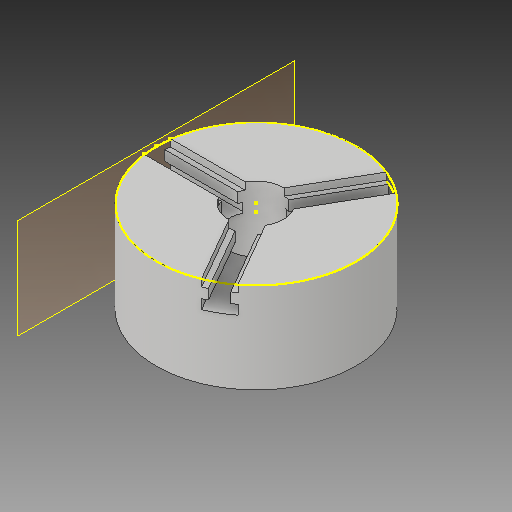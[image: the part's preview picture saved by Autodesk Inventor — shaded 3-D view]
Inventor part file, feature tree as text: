
AUTODESK INVENTOR PART (.ipt)
format: ipt  version: 2018 (Build 220112000, 112)  size: 259,584 bytes
history: native  units: in
note: dims shown in document units (in); Inventor stores cm internally (conversion verified against a paired STEP export)
features: sketch x13, extrude x11, plane x1, pattern_circular x1, projected_geometry x1
ambient origin geometry x8: Origin, YZ Plane, XZ Plane, XY Plane, X Axis, Y Axis, Z Axis, Center Point
bodies: Solid1 (feature_tree)
feature tree (27):
  extrude  "Extrusion1"  Depth=3.5787in
  extrude  "Extrusion2"  Depth=3.5787in
  sketch  "Sketch3"  dims[d13=1.1811in d15=360.0deg d17=0.2827in d18=0.0in]
  extrude  "Extrusion6"  Depth=0.2827in TaperAngle=0.0deg
  extrude  "Extrusion7"  Depth=0.3937in TaperAngle=0.0deg
  extrude  "Extrusion8"  Depth=0.3937in TaperAngle=0.0deg
  extrude  "Extrusion9"  Depth=0.3748in TaperAngle=0.0deg
  extrude  "Extrusion10"  Depth=0.3937in TaperAngle=0.0deg
  sketch  "Sketch12"  dims[d43=1.1811in d44=360.0deg d48=1.1811in d50=360.0deg]
  sketch  "Sketch13"  dims[d52=1.9685in d53=0.0in]
  plane  "Work Plane10"
  extrude  "Extrusion11"  Depth=1.1811in TaperAngle=360.0deg
  extrude  "Extrusion12"  [1 undecoded]
  extrude  "Extrusion13"  [1 undecoded]
  pattern_circular  "Circular Pattern1"  [2 undecoded]
  extrude  "Extrusion14"  [1 undecoded]
  sketch  "Sketch1"  dims[d1=3.5787in d2=0.0in d3=2.1701in]
  sketch  "Sketch2"  dims[d4=3.5787in d5=0.0in d6=0.5256in]
  sketch  "Sketch7"  dims[d19=0.3937in d20=0.0in d21=0.3937in d22=0.0in]
  sketch  "Sketch8"  dims[d23=0.3937in d24=0.0in d25=0.3937in d26=0.0in]
  sketch  "Sketch10"  dims[d36=0.3748in d37=2.9365in d38=0.0in]
  sketch  "Sketch11"  dims[d39=2.9365in d40=0.0in d41=0.3937in d42=0.0in]
  projected_geometry  "Projected Loop1"
  sketch  "Sketch16"
  sketch  "Sketch18"
  sketch  "Sketch20"
  sketch  "Sketch21"
note: 5 required parameter values undecoded (feature->parameter linkage not recoverable at this tier; creation-order binding heuristic only, values carry confidence <= 0.55)
